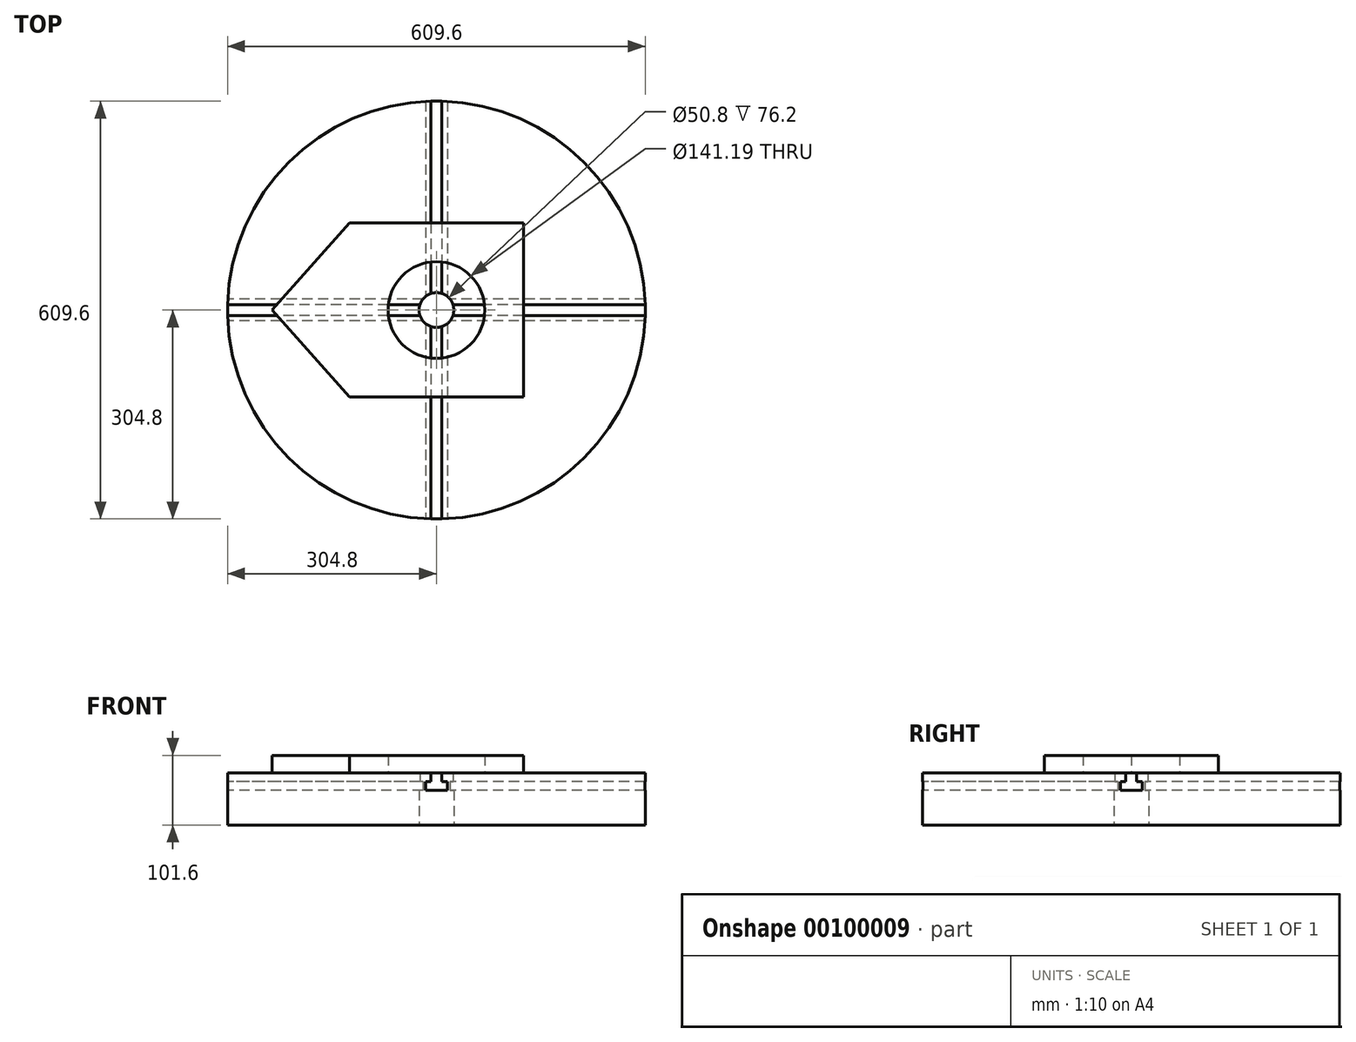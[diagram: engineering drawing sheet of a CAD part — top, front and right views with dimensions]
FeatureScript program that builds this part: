
annotation { "Feature Type Name" : "Feature", "Feature Type Description" : "" }
export const myFeature = defineFeature(function(context is Context, id is Id, definition is map)
    precondition{}
    {
        {
            var Q0;
            Q0=qCreatedBy(makeId("Top.planeOp"),FACE);
            var sketch = newSketch(context, id + "F0", { "sketchPlane" : qUnion([Q0])});
            skCircle(sketch, "E0", {"center": v(0, 0) * mm, "radius": 304.8 * mm});
            skCircle(sketch, "E1", {"center": v(0, 0) * mm, "radius": 25.4 * mm});
            skSolve(sketch);
        }
        {
            var Q0;
            Q0=qSketchRegion(id+"F0",true);
            extrude(context, id + "F1", {"entities" : qUnion([Q0]), "depth" : 76.2 * mm});
        }
        {
            var Q0;
            Q0=qCreatedBy(makeId("Front.planeOp"),FACE);
            var sketch = newSketch(context, id + "F2", { "sketchPlane" : qUnion([Q0])});
            skLineSegment(sketch, "E2", {"start": v(-7.94, 76.2) * mm, "end": v(-7.94, 63.5) * mm});
            skLineSegment(sketch, "E3", {"start": v(-7.94, 63.5) * mm, "end": v(-15.88, 63.5) * mm});
            skLineSegment(sketch, "E4", {"start": v(-15.88, 63.5) * mm, "end": v(-15.88, 50.8) * mm});
            skLineSegment(sketch, "E5", {"start": v(-15.88, 50.8) * mm, "end": v(15.88, 50.8) * mm});
            skLineSegment(sketch, "E6", {"start": v(15.88, 50.8) * mm, "end": v(15.88, 63.5) * mm});
            skLineSegment(sketch, "E7", {"start": v(15.88, 63.5) * mm, "end": v(7.94, 63.5) * mm});
            skLineSegment(sketch, "E8", {"start": v(7.94, 63.5) * mm, "end": v(7.94, 76.2) * mm});
            skLineSegment(sketch, "E9", {"start": v(7.94, 76.2) * mm, "end": v(-7.94, 76.2) * mm});
            skLineSegment(sketch, "E10", {"start": v(0, 0) * mm, "end": v(0, 117.73) * mm, "construction": true});
            skSolve(sketch);
        }
        {
            var Q0;
            Q0=makeQuery(id+"F2.imprint","IMPRINT",FACE,{"disambiguationData":[TD([[makeQuery(id+"F2.imprint","IMPRINT",EDGE,{"derivedFrom":sQuery(id+"F2.wireOp",EDGE,"E2")}),1.0]])]});
            extrude(context, id + "F3", {"entities" : qUnion([Q0]), "endBound" : BoundingType.THROUGH_ALL, "depth" : 25.4 * mm, "hasSecondDirection" : true, "secondDirectionBound" : SecondDirectionBoundingType.THROUGH_ALL, "secondDirectionOppositeDirection" : true, "secondDirectionDepth" : 25.4 * mm});
        }
        {
            var Q0;
            Q0=makeQuery(id+"F3.opExtrude","SWEPT_BODY",BODY,{"disambiguationData":[OSD([sQuery(id+"F2.wireOp",EDGE,"E2"),sQuery(id+"F2.wireOp",EDGE,"E3"),sQuery(id+"F2.wireOp",EDGE,"E4"),sQuery(id+"F2.wireOp",EDGE,"E5"),sQuery(id+"F2.wireOp",EDGE,"E6"),sQuery(id+"F2.wireOp",EDGE,"E7"),sQuery(id+"F2.wireOp",EDGE,"E8"),sQuery(id+"F2.wireOp",EDGE,"E9")])]});
            var Q1;
            Q1=sQuery(id+"F2.wireOp",EDGE,"E10");
            circularPattern(context, id + "F4", {"entities" : qUnion([Q0]), "axis" : qUnion([Q1]), "angle" : 90 * degree, "instanceCount" : 2});
        }
        {
            var Q0;
            Q0=makeQuery(id+"F4.opPattern","COPY",BODY,{"derivedFrom":makeQuery(id+"F3.opExtrude","SWEPT_BODY",BODY,{"disambiguationData":[OSD([sQuery(id+"F2.wireOp",EDGE,"E2"),sQuery(id+"F2.wireOp",EDGE,"E3"),sQuery(id+"F2.wireOp",EDGE,"E4"),sQuery(id+"F2.wireOp",EDGE,"E5"),sQuery(id+"F2.wireOp",EDGE,"E6"),sQuery(id+"F2.wireOp",EDGE,"E7"),sQuery(id+"F2.wireOp",EDGE,"E8"),sQuery(id+"F2.wireOp",EDGE,"E9")])]}),"instanceName":"1"});
            var Q1;
            Q1=makeQuery(id+"F3.opExtrude","SWEPT_BODY",BODY,{"disambiguationData":[OSD([sQuery(id+"F2.wireOp",EDGE,"E2"),sQuery(id+"F2.wireOp",EDGE,"E3"),sQuery(id+"F2.wireOp",EDGE,"E4"),sQuery(id+"F2.wireOp",EDGE,"E5"),sQuery(id+"F2.wireOp",EDGE,"E6"),sQuery(id+"F2.wireOp",EDGE,"E7"),sQuery(id+"F2.wireOp",EDGE,"E8"),sQuery(id+"F2.wireOp",EDGE,"E9")])]});
            var Q2;
            Q2=makeQuery(id+"F4.opPattern","COPY",BODY,{"derivedFrom":makeQuery(id+"F3.opExtrude","SWEPT_BODY",BODY,{"disambiguationData":[OSD([sQuery(id+"F2.wireOp",EDGE,"E2"),sQuery(id+"F2.wireOp",EDGE,"E3"),sQuery(id+"F2.wireOp",EDGE,"E4"),sQuery(id+"F2.wireOp",EDGE,"E5"),sQuery(id+"F2.wireOp",EDGE,"E6"),sQuery(id+"F2.wireOp",EDGE,"E7"),sQuery(id+"F2.wireOp",EDGE,"E8"),sQuery(id+"F2.wireOp",EDGE,"E9")])]}),"instanceName":"2"});
            var Q3;
            Q3=makeQuery(id+"F1.opExtrude","SWEPT_BODY",BODY,{"disambiguationData":[OSD([sQuery(id+"F0.wireOp",EDGE,"E0"),sQuery(id+"F0.wireOp",EDGE,"E1")])]});
            booleanBodies(context, id + "F5", {"operationType" : BooleanOperationType.SUBTRACTION, "tools" : qUnion([Q0, Q1, Q2]), "targets" : qUnion([Q3])});
        }
        {
            var Q0;
            {var subQ0=sQuery(id+"F0.wireOp",EDGE,"E0");var subQ1=sQuery(id+"F0.wireOp",EDGE,"E1");Q0=makeQuery(id+"F5.opBoolean","SPLIT",FACE,{"disambiguationData":[TD([makeQuery(id+"F1.opExtrude","SWEPT_FACE",FACE,{"disambiguationData":[OSD([subQ0])]}),makeQuery(id+"F1.opExtrude","SWEPT_FACE",FACE,{"disambiguationData":[OSD([subQ1])]}),makeQuery(id+"F3.opExtrude","SWEPT_FACE",FACE,{"disambiguationData":[OSD([sQuery(id+"F2.wireOp",EDGE,"E2")])]}),makeQuery(id+"F4.opPattern","COPY",FACE,{"derivedFrom":makeQuery(id+"F3.opExtrude","SWEPT_FACE",FACE,{"disambiguationData":[OSD([sQuery(id+"F2.wireOp",EDGE,"E8")])]}),"instanceName":"1"})])],"derivedFrom":makeQuery(id+"F1.opExtrude","CAP_FACE",FACE,{"disambiguationData":[OSD([subQ0,subQ1])],"isStart":false})});}
            var sketch = newSketch(context, id + "F6", { "sketchPlane" : qUnion([Q0])});
            skLineSegment(sketch, "E11.bottom", {"start": v(-127, 127) * mm, "end": v(127, 127) * mm});
            skLineSegment(sketch, "E11.top", {"start": v(-127, -127) * mm, "end": v(127, -127) * mm});
            skLineSegment(sketch, "E11.left", {"start": v(-127, 127) * mm, "end": v(-127, -127) * mm});
            skLineSegment(sketch, "E11.right", {"start": v(127, 127) * mm, "end": v(127, -127) * mm});
            skPoint(sketch, "E11.middle", {"position": v(0, 0) * mm});
            skLineSegment(sketch, "E12", {"start": v(-127, 127) * mm, "end": v(0, 240.08) * mm});
            skLineSegment(sketch, "E13", {"start": v(0, 240.08) * mm, "end": v(127, 127) * mm});
            skCircle(sketch, "E14", {"center": v(0, 0) * mm, "radius": 70.6 * mm});
            skSolve(sketch);
        }
        {
            var Q0;
            {var subQ1=sQuery(id+"F6.wireOp",EDGE,"E11.top");Q0=makeQuery(id+"F6.imprint","IMPRINT",FACE,{"disambiguationData":[TD([[makeQuery(id+"F6.imprint","IMPRINT",EDGE,{"derivedFrom":subQ1}),1.0]])]});}
            var Q1;
            {var subQ0=sQuery(id+"F6.wireOp",EDGE,"E11.left");var subQ8=sQuery(id+"F6.wireOp",EDGE,"E11.bottom");var subQ9=makeQuery(id+"F6.imprint","INTERSECT",VERTEX,{"derivedFrom":[subQ8,subQ0,sQuery(id+"F6.wireOp",EDGE,"E12")]});Q1=makeQuery(id+"F6.imprint","IMPRINT",FACE,{"disambiguationData":[TD([[makeQuery(id+"F6.imprint","IMPRINT",EDGE,{"disambiguationData":[TD([[subQ9,-1.0]])],"derivedFrom":subQ8}),-1.0]])]});}
            var Q2;
            {var subQ0=sQuery(id+"F6.wireOp",EDGE,"E12");var subQ1=sQuery(id+"F6.wireOp",EDGE,"E11.bottom");var subQ2=makeQuery(id+"F6.imprint","INTERSECT",VERTEX,{"derivedFrom":[subQ1,sQuery(id+"F6.wireOp",EDGE,"E11.left"),subQ0]});Q2=makeQuery(id+"F6.imprint","IMPRINT",FACE,{"disambiguationData":[TD([[makeQuery(id+"F6.imprint","IMPRINT",EDGE,{"disambiguationData":[TD([[subQ2,-1.0]])],"derivedFrom":subQ1}),1.0]])]});}
            var Q3;
            {var subQ0=sQuery(id+"F6.wireOp",EDGE,"E13");Q3=makeQuery(id+"F6.imprint","IMPRINT",FACE,{"disambiguationData":[TD([[makeQuery(id+"F6.imprint","IMPRINT",EDGE,{"derivedFrom":subQ0}),-1.0]])]});}
            extrude(context, id + "F7", {"entities" : qUnion([Q0, Q1, Q2, Q3]), "depth" : 25.4 * mm});
        }
        {
            var Q0;
            Q0=makeQuery(id+"F1.opExtrude","SWEPT_BODY",BODY,{"disambiguationData":[OSD([sQuery(id+"F0.wireOp",EDGE,"E0"),sQuery(id+"F0.wireOp",EDGE,"E1")])]});
            var Q1;
            Q1=makeQuery(id+"F7.opExtrude","SWEPT_BODY",BODY,{"disambiguationData":[OSD([sQuery(id+"F6.wireOp",EDGE,"E11.top"),sQuery(id+"F6.wireOp",EDGE,"E11.left"),sQuery(id+"F6.wireOp",EDGE,"E11.right"),sQuery(id+"F6.wireOp",EDGE,"E12"),sQuery(id+"F6.wireOp",EDGE,"E13"),sQuery(id+"F6.wireOp",EDGE,"E14")])]});
            var Q2;
            Q2=sQuery(id+"F2.wireOp",EDGE,"E10");
            transform(context, id + "F8", {"entities" : qUnion([Q0, Q1]), "transformType" : TransformType.ROTATION, "transformAxis" : qUnion([Q2]), "angle" : 90 * degree, "makeCopy" : false});
        }
    });
